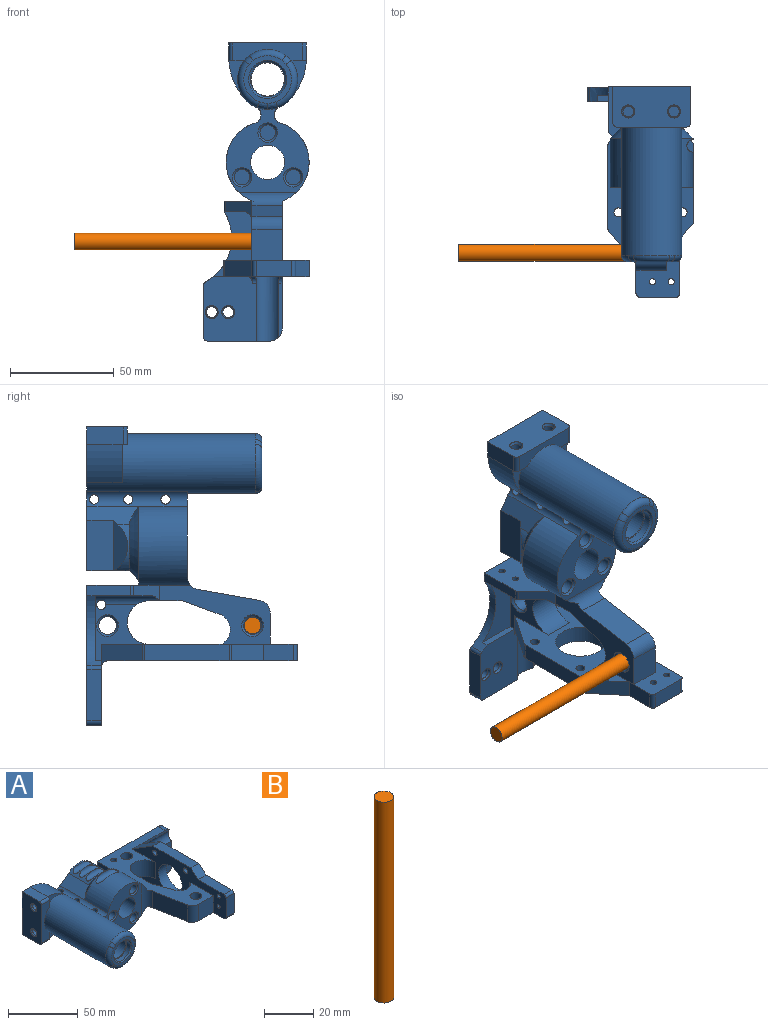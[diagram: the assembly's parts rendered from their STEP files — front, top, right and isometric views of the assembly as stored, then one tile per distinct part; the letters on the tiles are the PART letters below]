
ASSEMBLY  parts=2 mates=1
PART A: 150 faces, bbox 144.7x102.4x51.9 mm
  f0: cylinder r=2.6mm len=5.75mm, axis (0,-1,0), area 93.9mm2, adj f1,f2
  f1: bspline ~6.81x6.22mm, area 23.1mm2, adj f0,f3
  f2: plane 67.5x38mm, normal (0,1,0), area 2090.1mm2, adj f0,f4,f5,f6,f7,f8,f9,f10
  f3: cone r=2.15mm half-angle=45deg, axis (0,-1,0), area 1.5mm2, adj f1,f14
  f4: plane 30x7mm, normal (1,0,0), area 196mm2, adj f2,f5,f6,f14,f15
  f5: cylinder r=2mm len=7mm, axis (0,-1,0), area 22mm2, adj f2,f4,f7,f14
  f6: cylinder r=6mm len=7mm, axis (0,1,0), area 59.2mm2, adj f2,f4,f8,f15,f16
  f7: plane 24.77x7mm, normal (0,0,-1), area 173.4mm2, adj f2,f5,f9,f14
  f8: plane 88.5x61.5mm, normal (0,0,1), area 1551.2mm2, adj f2,f6,f12,f16,f17,f20,f21,f22
  f9: cylinder r=2mm len=7mm, axis (0,-1,0), area 15.1mm2, adj f2,f7,f10,f14
  f10: cylinder r=24mm len=33.97mm, axis (0,1,0), area 171mm2, adj f2,f9,f11,f14,f18,f19
  f11: plane 21.1x5mm, normal (0,0,-1), area 105.5mm2, adj f2,f10,f12,f33,f34
  f12: plane 50.03x28mm, normal (-1,0,0), area 746.4mm2, adj f2,f8,f11,f23,f34,f35,f36,f37
  f13: cylinder r=2.6mm len=5.75mm, axis (0,-1,0), area 93.9mm2, adj f2,f39
  f14: plane 39x25.8mm, normal (0,-1,0), area 724.1mm2, adj f3,f4,f5,f7,f9,f10,f15,f19
  f15: cylinder r=6mm len=38mm, axis (1,0,0), area 653.2mm2, adj f4,f6,f14,f16,f41,f42,f43,f44
  f16: plane 26.29x1.8mm, normal (0,-1,0), area 45mm2, adj f6,f8,f15,f43
  f17: plane 8x0.29mm, normal (0,1,0), area 2.3mm2, adj f8,f20,f41,f48
  f18: plane 31.5x18.67mm, normal (0,-1,0), area 368.4mm2, adj f10,f19,f33,f46,f49,f50
  f19: plane 18.67x3mm, normal (-1,0,0), area 56mm2, adj f10,f14,f18,f46
  f20: plane 94.5x41.06mm, normal (-1,0,0), area 1877.2mm2, adj f8,f17,f22,f28,f29,f37,f45,f46
  f21: cylinder r=20mm len=38.1mm, axis (0,1,0), area 1079.6mm2, adj f8,f23,f35,f57,f58,f59
  f22: cylinder r=10.5mm len=21mm, axis (0,0,1), area 481.7mm2, adj f8,f20,f24,f46,f50
  f23: cylinder r=6.33mm len=27.32mm, axis (0,0,-1), area 159.1mm2, adj f8,f12,f21,f25,f36,f37,f58
  f24: plane 16x15.01mm, normal (1,0,0), area 235.1mm2, adj f8,f22,f26,f37,f38,f50
  f25: plane 29.54x14.56mm, normal (-0.98,-0.17,0), area 436.8mm2, adj f8,f23,f27,f37
  f26: plane 18.79x14.56mm, normal (0.94,0.34,0), area 291.2mm2, adj f8,f24,f28,f37
  f27: cylinder r=6.33mm len=14.56mm, axis (0,0,-1), area 128.6mm2, adj f8,f25,f29,f37
  f28: cylinder r=8mm len=14.56mm, axis (0,0,1), area 253.1mm2, adj f8,f20,f26,f37
  f29: plane 14.95x14.56mm, normal (0,-1,0), area 217.7mm2, adj f8,f20,f27,f37
  f30: cylinder r=4.25mm len=13.56mm, axis (0,0,-1), area 349.7mm2, adj f8,f60,f61
  f31: cylinder r=4.25mm len=13.56mm, axis (0,0,-1), area 349.7mm2, adj f8,f62,f63,f64
  f32: cylinder r=2.25mm len=15.14mm, axis (0,0,1), area 207.8mm2, adj f8,f46,f50
  f33: plane 26.69x9mm, normal (1,0,0), area 187.4mm2, adj f11,f18,f34,f38,f50,f65,f66
  f34: cylinder r=2mm len=5mm, axis (-1,0,0), area 8mm2, adj f11,f12,f33,f38
  f35: plane 40x38.1mm, normal (0,1,0), area 49.7mm2, adj f12,f21,f36,f67,f68,f69,f70,f71
  f36: cylinder r=20mm len=38.1mm, axis (0,1,0), area 1195.8mm2, adj f12,f23,f35,f58,f72
  f37: plane 53.5x28.5mm, normal (0,0,-1), area 641.7mm2, adj f12,f20,f23,f24,f25,f26,f27,f28
  f38: plane 13.55x13.18mm, normal (0,-0.72,-0.7), area 95mm2, adj f12,f24,f33,f34,f37,f50
  f39: bspline ~6.81x6.22mm, area 23.1mm2, adj f13,f40
  f40: cone r=2.15mm half-angle=45deg, axis (0,-1,0), area 1.5mm2, adj f14,f39
  f41: plane 94.5x41.06mm, normal (1,0,0), area 2338.5mm2, adj f8,f15,f17,f42,f43,f45,f48,f51
  f42: cylinder r=3mm len=4.16mm, axis (0,0,-1), area 12.9mm2, adj f14,f15,f41,f45
  f43: cylinder r=3mm len=3mm, axis (0,0,-1), area 6.6mm2, adj f8,f15,f16,f41
  f44: plane 12x12mm, normal (1,0,0), area 98.6mm2, adj f15,f61
  f45: plane 20.69x14.23mm, normal (0,0.56,-0.83), area 193.8mm2, adj f14,f20,f41,f42,f47,f75
  f46: plane 27.06x26mm, normal (0,0,-1), area 259.6mm2, adj f14,f18,f19,f20,f22,f32,f47,f50
  f47: plane 0.33x0.22mm, normal (1,0,0), area 0mm2, adj f14,f45,f46
  f48: plane 20.35x12.71mm, normal (0,0.53,0.85), area 191.9mm2, adj f17,f20,f41,f54
  f49: plane 2.24x0.5mm, normal (-1,0,0), area 0.8mm2, adj f18,f65
  f50: cylinder r=4.44mm len=30.57mm, axis (0,-1,0), area 178.3mm2, adj f18,f22,f24,f32,f33,f38,f46
  f51: cylinder r=12mm len=24mm, axis (1,0,0), area 603.2mm2, adj f20,f41
  f52: plane 26.07x8mm, normal (0,0,1), area 208.5mm2, adj f20,f41,f53,f98
  f53: plane 8x7.66mm, normal (0,-0.64,0.77), area 80mm2, adj f20,f41,f52,f54
  f54: plane 38.43x8mm, normal (0,0,1), area 307.4mm2, adj f20,f41,f48,f53
  f55: cylinder r=2.15mm len=8mm, axis (1,0,0), area 108.1mm2, adj f20,f41
  f56: cylinder r=2.15mm len=8mm, axis (1,0,0), area 108.1mm2, adj f20,f41
  f57: cylinder r=4.31mm len=48.5mm, axis (0,1,0), area 348.6mm2, adj f21,f58,f71,f83,f84,f85,f86,f87
  f58: plane 41x40mm, normal (0,-1,0), area 778.3mm2, adj f21,f23,f36,f57,f72,f84,f88,f89
  f59: cylinder r=3mm len=21.07mm, axis (1,0,0), area 153.1mm2, adj f21
  f60: cone r=4.25mm half-angle=45deg, axis (0,0,-1), area 42.2mm2, adj f30,f46
  f61: cylinder r=2.15mm len=6.33mm, axis (1,0,0), area 79.6mm2, adj f30,f44
  f62: cone r=4.25mm half-angle=45deg, axis (0,0,-1), area 34.9mm2, adj f31,f37,f64
  f63: cylinder r=2.15mm len=6.33mm, axis (1,0,0), area 79.6mm2, adj f31,f92
  f64: cone r=4.39mm half-angle=45deg, axis (0,0,-1), area 7.3mm2, adj f31,f37,f62
  f65: cylinder r=1.5mm len=5mm, axis (-1,0,0), area 47.1mm2, adj f12,f33,f49
  f66: cylinder r=1.5mm len=5mm, axis (-1,0,0), area 47.1mm2, adj f12,f33
  f67: cone r=15.42mm half-angle=45deg, axis (0,-1,0), area 231.8mm2, adj f35,f68,f69,f93
  f68: plane 23.36x4.8mm, normal (0.71,0.71,0), area 138.9mm2, adj f35,f67,f70,f96
  f69: plane 25x8.96mm, normal (-0.58,0,-0.81), area 205.6mm2, adj f35,f67,f72,f83,f93,f94,f95
  f70: cone r=15.42mm half-angle=45deg, axis (0,-1,0), area 231.8mm2, adj f35,f68,f71,f97
  f71: plane 25x8.96mm, normal (-0.58,0,0.81), area 244.9mm2, adj f35,f57,f70,f83,f97
  f72: cylinder r=4.31mm len=48.5mm, axis (0,1,0), area 348.6mm2, adj f36,f58,f69,f83,f84,f85,f86,f87
  f73: cylinder r=2mm len=8mm, axis (-1,0,0), area 11.2mm2, adj f20,f41,f74,f77
  f74: plane 40.66x8mm, normal (0,0,-1), area 325.3mm2, adj f20,f41,f73,f75
  f75: cylinder r=2mm len=8mm, axis (-1,0,0), area 9.5mm2, adj f20,f41,f45,f74
  f76: plane 14.07x8mm, normal (0,0,-1), area 112.5mm2, adj f20,f41,f77,f120
  f77: plane 15.53x13.03mm, normal (0,-0.64,-0.77), area 162.2mm2, adj f20,f41,f73,f76
  f78: cylinder r=6mm len=12mm, axis (1,0,0), area 263.9mm2, adj f41,f92
  f79: cylinder r=2.15mm len=8mm, axis (1,0,0), area 108.1mm2, adj f20,f41
  f80: cylinder r=2.15mm len=8mm, axis (1,0,0), area 108.1mm2, adj f20,f41
  f81: cylinder r=1.5mm len=8mm, axis (1,0,0), area 75.4mm2, adj f20,f41
  f82: cylinder r=1.5mm len=8mm, axis (1,0,0), area 75.4mm2, adj f20,f41
  f83: plane 69.38x37.5mm, normal (0,1,0), area 1234.7mm2, adj f57,f69,f71,f72,f84,f89,f94,f96
  f84: cylinder r=14.5mm len=81.5mm, axis (0,1,0), area 5754.6mm2, adj f57,f58,f72,f83,f103,f104,f105,f106
  f85: cylinder r=2.25mm len=7.95mm, axis (0,0,1), area 108.4mm2, adj f57,f72
  f86: cylinder r=2.25mm len=7.95mm, axis (0,0,1), area 108.4mm2, adj f57,f72
  f87: cylinder r=2.25mm len=7.95mm, axis (0,0,1), area 108.4mm2, adj f57,f72
  f88: cone r=3.7mm half-angle=45deg, axis (0,-1,0), area 37.3mm2, adj f58,f107
  f89: cylinder r=8.2mm len=48.5mm, axis (0,1,0), area 2498.8mm2, adj f58,f83
  f90: cone r=3.7mm half-angle=45deg, axis (0,-1,0), area 37.3mm2, adj f58,f110
  f91: cone r=3.7mm half-angle=45deg, axis (0,-1,0), area 37.3mm2, adj f58,f111
  f92: plane 12x12mm, normal (1,0,0), area 98.6mm2, adj f63,f78
  f93: cylinder r=15.42mm len=22.14mm, axis (0,1,0), area 65.3mm2, adj f67,f69,f95,f96
  f94: plane 24.43x13mm, normal (0,0,-1), area 317.5mm2, adj f69,f83,f95,f96
  f95: plane 24.43x6.75mm, normal (0,0.64,-0.77), area 147.4mm2, adj f69,f93,f94,f96
  f96: plane 20.45x20mm, normal (1,0,0), area 405.7mm2, adj f68,f83,f93,f94,f95,f97
  f97: cylinder r=15.42mm len=22.14mm, axis (0,1,0), area 205.4mm2, adj f70,f71,f83,f96,f112,f113,f114
  f98: cylinder r=2mm len=8mm, axis (-1,0,0), area 25.1mm2, adj f20,f41,f52,f119
  f99: plane 17.5x8.5mm, normal (0,0,-1), area 148.8mm2, adj f83,f100,f115,f117,f121
  f100: plane 37.5x19.5mm, normal (-1,0,0), area 667.2mm2, adj f83,f99,f101,f121,f122,f123,f124,f125
  f101: plane 17.5x8.5mm, normal (0,0,1), area 148.8mm2, adj f83,f100,f103,f105,f124
  f102: cone r=8.2mm half-angle=45deg, axis (0,1,0), area 70mm2, adj f83,f126
  f103: cylinder r=30mm len=18.3mm, axis (0,1,0), area 342.6mm2, adj f83,f84,f101,f104
  f104: plane 18.3x7.5mm, normal (0,-1,0), area 50.2mm2, adj f84,f103,f105
  f105: plane 7.5x2.5mm, normal (1,0,0), area 17.9mm2, adj f84,f101,f104,f123,f124
  f106: torus R=11.5mm, axis (0,-1,0), area 120.2mm2, adj f84,f109,f129,f130
  f107: cylinder r=3.7mm len=9mm, axis (0,-1,0), area 209.2mm2, adj f88,f131
  f108: revolved ~5x3.71mm, area 22.2mm2, adj f84,f109,f118,f130
  f109: revolved ~5x3.71mm, area 22.2mm2, adj f84,f106,f108,f130
  f110: cylinder r=3.7mm len=9mm, axis (0,-1,0), area 209.2mm2, adj f90,f132
  f111: cylinder r=3.7mm len=9mm, axis (0,-1,0), area 209.2mm2, adj f91,f133
  f112: cylinder r=3mm len=18.05mm, axis (1,0,0), area 129.3mm2, adj f97
  f113: cylinder r=3mm len=18.05mm, axis (1,0,0), area 129.3mm2, adj f97
  f114: cylinder r=3mm len=18.05mm, axis (1,0,0), area 129.3mm2, adj f97
  f115: plane 7.5x2.5mm, normal (1,0,0), area 17.9mm2, adj f84,f99,f116,f121,f123
  f116: plane 18.3x7.5mm, normal (0,-1,0), area 50.2mm2, adj f84,f115,f117
  f117: cylinder r=30mm len=18.3mm, axis (0,1,0), area 342.6mm2, adj f83,f84,f99,f116
  f118: torus R=11.5mm, axis (0,-1,0), area 120.2mm2, adj f84,f108,f127,f130
  f119: plane 17.13x8mm, normal (0,-1,0), area 137.1mm2, adj f20,f41,f98,f120
  f120: cylinder r=2mm len=8mm, axis (-1,0,0), area 25.1mm2, adj f20,f41,f76,f119
  f121: cylinder r=2mm len=8.5mm, axis (1,0,0), area 26.7mm2, adj f99,f100,f115,f123
  f122: cone r=2.15mm half-angle=45deg, axis (-1,0,0), area 0.5mm2, adj f100,f134
  f123: plane 33.5x8.5mm, normal (0,-1,0), area 200.9mm2, adj f84,f100,f105,f115,f121,f124
  f124: cylinder r=2mm len=8.5mm, axis (1,0,0), area 26.7mm2, adj f100,f101,f105,f123
  f125: cone r=2.15mm half-angle=45deg, axis (-1,0,0), area 0.5mm2, adj f100,f135
  f126: cylinder r=8.3mm len=16.6mm, axis (0,1,0), area 187.7mm2, adj f102,f136
  f127: revolved ~4.28x4.28mm, area 15mm2, adj f84,f118,f128,f130
  f128: torus R=11.5mm, axis (0,-1,0), area 82.3mm2, adj f84,f127,f129,f130
  f129: revolved ~4.28x4.28mm, area 15mm2, adj f84,f106,f128,f130
  f130: plane 23x23mm, normal (0,-1,0), area 149.6mm2, adj f106,f108,f109,f118,f127,f128,f129,f137
  f131: plane 7.4x7.4mm, normal (0,-1,0), area 43mm2, adj f107
  f132: plane 7.4x7.4mm, normal (0,-1,0), area 43mm2, adj f110
  f133: plane 7.4x7.4mm, normal (0,-1,0), area 43mm2, adj f111
  f134: revolved ~6.26x6.26mm, area 24.9mm2, adj f122,f138
  f135: revolved ~6.26x6.26mm, area 24.9mm2, adj f125,f139
  f136: plane 16.6x16.6mm, normal (0,1,0), area 15.4mm2, adj f126,f140
  f137: cone r=8.2mm half-angle=45deg, axis (0,-1,0), area 67.6mm2, adj f130,f141,f142
  f138: cylinder r=2.6mm len=6.7mm, axis (-1,0,0), area 109.5mm2, adj f134,f143
  f139: cylinder r=2.6mm len=6.7mm, axis (-1,0,0), area 109.5mm2, adj f135,f144
  f140: cylinder r=8mm len=16mm, axis (0,1,0), area 30.2mm2, adj f136,f145
  f141: cone r=9.06mm half-angle=45deg, axis (0,-1,0), area 2.4mm2, adj f130,f137,f142
  f142: cylinder r=8.3mm len=16.6mm, axis (0,-1,0), area 187.7mm2, adj f137,f141,f146
  f143: plane 5.2x5.2mm, normal (-1,0,0), area 21.2mm2, adj f138
  f144: plane 5.2x5.2mm, normal (-1,0,0), area 21.2mm2, adj f139
  f145: plane 16.6x16.6mm, normal (0,-1,0), area 15.4mm2, adj f140,f147
  f146: plane 16.6x16.6mm, normal (0,-1,0), area 15.4mm2, adj f142,f148
  f147: cylinder r=8.3mm len=74.3mm, axis (0,-1,0), area 3874.8mm2, adj f145,f149
  f148: cylinder r=8mm len=16mm, axis (0,-1,0), area 30.2mm2, adj f146,f149
  f149: plane 16.6x16.6mm, normal (0,1,0), area 15.4mm2, adj f147,f148
PART B: 3 faces, bbox 8x8x100 mm
  f0: cylinder r=4mm len=100mm, axis (0,0,-1), area 2513.3mm2, adj f1,f2
  f1: plane 8x8mm, normal (0,0,1), area 50.3mm2, adj f0
  f2: plane 8x8mm, normal (0,0,-1), area 50.3mm2, adj f0
PLACE A rot(axis=(0,1,0),90deg) t=(-123.32,1.15,87.03)mm
PLACE B rot(axis=(0.58,0.58,0.58),120deg) t=(-216.32,-78.85,-8.85)mm
MATE fastened B.f0 <-> A.f62  axis (1,0,0) through (-116.32,-78.85,-8.85)mm
